# Revit family: BIMLIB_Балансировочный_клапан_Auto_РОСТерм
name_source: partatom
category: Арматура трубопроводов
revit_build: Autodesk Revit 2017 (Build: 20170118_1100(x64)
units: mm (PartAtom-declared; Revit-internal decimal feet)

## family parameters
Всегда вертикально = Нет
На основе рабочей плоскости = Нет
Общий = Нет
При загрузке вырезать с полостями = Нет
Размер круглого соединителя = Использовать диаметр
Тип детали = Клапан - Вставляется

## types (1)
- HEIZEN AUTO
    ADSK_URL документации изделия = http://rostherm.ru
    ADSK_URL страницы изделия = http://rostherm.ru
    ADSK_Версия Revit = 2017
    ADSK_Единица измерения = шт.
    ADSK_Завод-изготовитель = Heizen
    BL_BIM library = https://bimlib.pro
    DN15 = BIMLIB_Балансировочный_клапан_Auto_РОСТерм_DN15 : DN15
    DN20 = BIMLIB_Балансировочный_клапан_Auto_РОСТерм_DN20 : DN20
    DN25 = BIMLIB_Балансировочный_клапан_Auto_РОСТерм_DN25 : DN25
    DN32 = BIMLIB_Балансировочный_клапан_Auto_РОСТерм_DN32 : DN32
    DN40 = BIMLIB_Балансировочный_клапан_Auto_РОСТерм_DN40 : DN40
    DN50 = BIMLIB_Балансировочный_клапан_Auto_РОСТерм_DN50 : DN50
    URL = http://rostherm.ru
    Изготовитель = РОСТерм
    Коэффициент K = 0
    Метод определения потерь = Не задано
    Описание = Автоматические балансировочные клапаны-регуляторы перепада давления HEIZEN Auto применяются для гидравлической балансировки, регулирования и ограничения расхода теплоносителя в системах отопления, холодоснабжения и кондиционирования. Клапаны обеспечивают гидравлическую балансировку путем поддержания перепада давления на постоянном уровне, вне зависимости от меняющихся характеристик расхода в системе.
    РТ_Материал_КорпусКлапана = BIMLIB_Латунь_РТ
    РТ_Материал_ЭлементРукоятки = BIMLIB_Пластик_черный_РТ
    РТ_Материал_ЭлементыКорпуса = BIMLIB_Пластик_красный_РТ
    РТ_Номинальное давление = 25.0 бары
